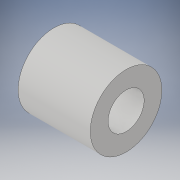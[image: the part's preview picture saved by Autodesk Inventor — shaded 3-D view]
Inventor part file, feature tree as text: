
AUTODESK INVENTOR PART (.ipt)
format: ipt  version: 2017 (Build 210142000, 142)  size: 94,720 bytes
history: native  units: in
note: dims shown in document units (in); Inventor stores cm internally (conversion verified against a paired STEP export)
features: extrude x1, sketch x1
ambient origin geometry x8: Origin, YZ Plane, XZ Plane, XY Plane, X Axis, Y Axis, Z Axis, Center Point
bodies: Solid1 (feature_tree)
feature tree (2):
  extrude  "Extrusion1"  Depth=0.375in
  sketch  "Sketch1"  dims[d0=0.1875in d1=0.372in d2=0.375in d3=0.0in]
